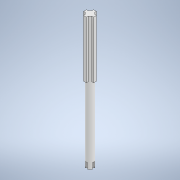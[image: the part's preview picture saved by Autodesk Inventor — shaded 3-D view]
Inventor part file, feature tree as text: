
AUTODESK INVENTOR PART (.ipt)
format: ipt  version: 2022 (Build 260153000, 153)  size: 166,400 bytes
history: native  units: in
note: dims shown in document units (in); Inventor stores cm internally (conversion verified against a paired STEP export)
features: extrude x3, sketch x3
ambient origin geometry x8: Origin, YZ Plane, XZ Plane, XY Plane, X Axis, Y Axis, Z Axis, Center Point
bodies: Body1 (feature_tree)
feature tree (6):
  extrude  "Extrusion7"  Depth=5.1181in TaperAngle=0.0deg
  extrude  "Extrusion8"  Depth=0.1181in
  extrude  "Extrusion9"  Depth=0.1181in
  sketch  "Sketch7"  dims[d71=0.2953in d72=5.1181in d73=0.0in]
  sketch  "Sketch8"  dims[d74=0.1181in d75=0.1181in]
  sketch  "Sketch9"  dims[d76=0.1181in d77=0.1181in d78=0.1181in d79=0.1181in d80=0.1181in d81=0.1181in d82=0.3937in d83=0.0in d84=1.9685in d85=0.0in d86=0.0787in d87=0.0787in d88=0.0787in d89=0.0787in d90=0.0787in d91=0.0787in d92=0.0787in d93=0.0787in d94=0.2362in d95=0.0in]
